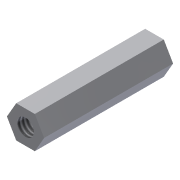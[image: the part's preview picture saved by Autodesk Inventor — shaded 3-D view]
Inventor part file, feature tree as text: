
AUTODESK INVENTOR PART (.ipt)
format: ipt  version: 2013 (Build 170138000, 138)  size: 81,920 bytes
history: native  units: in
note: dims shown in document units (in); Inventor stores cm internally (conversion verified against a paired STEP export)
features: sketch x2, extrude x1, hole x1, mirror x1
ambient origin geometry x8: Origin, YZ Plane, XZ Plane, XY Plane, X Axis, Y Axis, Z Axis, Center Point
bodies: Solid1 (feature_tree)
feature tree (5):
  extrude  "Extrusion1"  Depth=1.0in TaperAngle=0.0deg
  hole  "Hole1"  [1 undecoded]
  mirror  "Mirror1"
  sketch  "Sketch1"  dims[d0=0.25in d1=1.0in d2=0.0in]
  sketch  "Sketch2"  dims[d3=0.13in d4=0.375in d5=0.375in d6=0.25in d7=0.5635in d8=0.375in d9=0.0in]
note: 1 required parameter value undecoded (feature->parameter linkage not recoverable at this tier; creation-order binding heuristic only, values carry confidence <= 0.55)
